# Revit family: Towel_Ring-American_Standard-Delancey-7052190_Series
name_source: partatom
category: Specialty Equipment
units: mm (PartAtom-declared; Revit-internal decimal feet)

## family parameters
Cut with Voids When Loaded = No
Host = Face
OmniClass Number = 23.40.20.21.27
OmniClass Title = Towel Bars
Part Type = Normal
Room Calculation Point = No
Round Connector Dimension = Use Diameter
Shared = Yes

## types (5) — shared parameters
Assembly Code = C1030220
Default Elevation = 44"
Description = Delancey Towel Ring
Height = 8 1/4"
Installation Instruction Link = https://lixil.cdn.celum.cloud
Installation Type = Wall Mounted
Length = 2 7/8"
Manufacturer = American Standard
Price = Prices may vary. Please consult Manufacturer Representative for most up-to-date price list.
Product Documentation Link = https://lixil.cdn.celum.cloud
Product Page URL = https://www.americanstandard-us.com
Revised Date = 02/19/2024
URL = http://www.americanstandard-us.com
Warranty Information = Lifetime Warranty
Width = 7"

## per-type parameters (varying)
| type | Finish | Material |
| 7052190.002 | Metal-American Standard-002-Polished Chrome | Metal-American Standard-013-Polished Nickel PVD |
| 7052190.295 | Metal-American Standard-295-Brushed Nickel | Metal-American Standard-295-Brushed Nickel |
| 7052190.013 | Metal-American Standard-013-Polished Nickel PVD | Metal-American Standard-013-Polished Nickel |
| 7052190.278 | Metal-American Standard-278-Legacy Bronze | Metal-American Standard-278-Legacy Bronze |
| 7052190.GN0 | Metal-American Standard-GN0-Brushed Cool Sunrise | Metal-American Standard-GN0-Brushed Cool SunriseMetal-American Standard-GN0-Brushed Cool Sunrise |

note: column(s) folded — value = type name in every type: Model

## geometry (parser evidence)
native form markers: Sweep x3
no freeform markers — native parametric forms only
